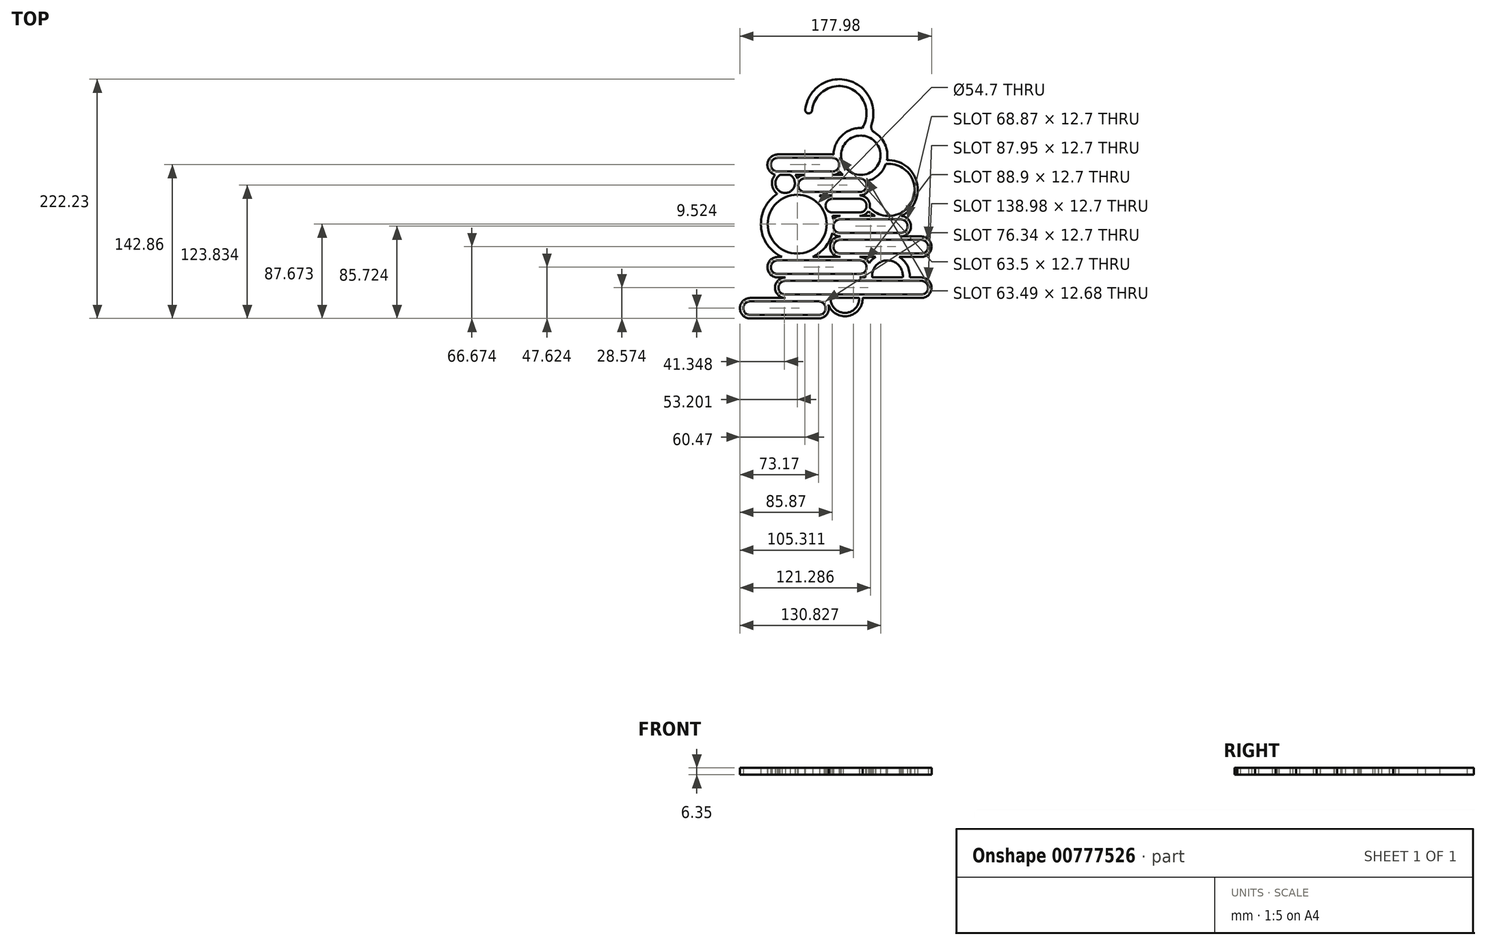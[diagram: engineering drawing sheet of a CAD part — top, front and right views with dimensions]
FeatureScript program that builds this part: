
annotation { "Feature Type Name" : "Feature", "Feature Type Description" : "" }
export const myFeature = defineFeature(function(context is Context, id is Id, definition is map)
    precondition{}
    {
        {
            var Q0;
            Q0=qCreatedBy(makeId("Top.planeOp"),FACE);
            var sketch = newSketch(context, id + "F0", { "sketchPlane" : qUnion([Q0])});
            skLineSegment(sketch, "E0", {"start": v(-38.1, 0) * mm, "end": v(-38.1, -172.32) * mm, "construction": true});
            skArc(sketch, "E1", {"start": v(-38.1, -25.4) * mm, "mid": v(-44.45, -31.75) * mm, "end": v(-38.1, -38.1) * mm});
            skArc(sketch, "E2", {"start": v(-38.1, -22.23) * mm, "mid": v(-47.55, -30.58) * mm, "end": v(-40.43, -40.99) * mm});
            skLineSegment(sketch, "E3", {"start": v(-63.64, -22.23) * mm, "end": v(0, -22.23) * mm, "construction": true});
            skLineSegment(sketch, "E4", {"start": v(-38.1, -22.23) * mm, "end": v(-17.96, -22.23) * mm});
            skLineSegment(sketch, "E5", {"start": v(-35.9, -41.26) * mm, "end": v(-26.48, -41.26) * mm});
            skLineSegment(sketch, "E6", {"start": v(0, 0) * mm, "end": v(-46.92, 0) * mm, "construction": true});
            skLineSegment(sketch, "E7", {"start": v(0, 0) * mm, "end": v(39.73, 0) * mm, "construction": true});
            skLineSegment(sketch, "E8", {"start": v(0, 0) * mm, "end": v(0, -203.37) * mm, "construction": true});
            skLineSegment(sketch, "E9", {"start": v(38.1, 0) * mm, "end": v(38.1, -151.12) * mm, "construction": true});
            skArc(sketch, "E10", {"start": v(38.1, -60.31) * mm, "mid": v(39.65, -60.18) * mm, "end": v(41.15, -59.8) * mm});
            skArc(sketch, "E11", {"start": v(37.6, -57.12) * mm, "mid": v(44.45, -51.02) * mm, "end": v(38.07, -44.44) * mm});
            skLineSegment(sketch, "E12", {"start": v(-35.9, -41.26) * mm, "end": v(-26.48, -41.26) * mm, "construction": true});
            skLineSegment(sketch, "E13", {"start": v(38.1, -50.79) * mm, "end": v(0, -50.79) * mm, "construction": true});
            skLineSegment(sketch, "E14", {"start": v(13.22, -41.26) * mm, "end": v(22.57, -41.26) * mm});
            skLineSegment(sketch, "E15", {"start": v(12.7, -60.31) * mm, "end": v(0.69, -60.31) * mm});
            skLineSegment(sketch, "E16", {"start": v(0, -44.44) * mm, "end": v(38.07, -44.44) * mm});
            skLineSegment(sketch, "E17", {"start": v(37.6, -57.12) * mm, "end": v(0, -57.12) * mm});
            skLineSegment(sketch, "E18", {"start": v(12.7, 0) * mm, "end": v(12.7, -99.3) * mm, "construction": true});
            skArc(sketch, "E19", {"start": v(13.22, -41.26) * mm, "mid": v(16.77, -40.36) * mm, "end": v(19.71, -38.2) * mm});
            skLineSegment(sketch, "E20", {"start": v(-12.7, 0) * mm, "end": v(-12.7, -99.53) * mm, "construction": true});
            skLineSegment(sketch, "E21", {"start": v(0, -44.44) * mm, "end": v(-47.76, -44.44) * mm, "construction": true});
            skArc(sketch, "E22", {"start": v(-12.73, -44.44) * mm, "mid": v(-19.05, -50.56) * mm, "end": v(-13.2, -57.12) * mm});
            skArc(sketch, "E23", {"start": v(-12.7, -41.26) * mm, "mid": v(-16.6, -42.1) * mm, "end": v(-19.83, -44.47) * mm});
            skLineSegment(sketch, "E24", {"start": v(0, -44.44) * mm, "end": v(-12.73, -44.44) * mm});
            skLineSegment(sketch, "E25", {"start": v(0, -57.12) * mm, "end": v(-13.2, -57.12) * mm});
            skLineSegment(sketch, "E26.trimOffspring", {"start": v(13.22, -41.26) * mm, "end": v(22.57, -41.26) * mm, "construction": true});
            skPoint(sketch, "E27.start.orphan", {"position": v(0, -41.38) * mm});
            skPoint(sketch, "E28.start.orphan", {"position": v(0, -28.68) * mm});
            skArc(sketch, "E29", {"start": v(12.7, -38.1) * mm, "mid": v(19.05, -31.75) * mm, "end": v(12.7, -25.4) * mm});
            skLineSegment(sketch, "E30", {"start": v(-38.1, -25.4) * mm, "end": v(12.7, -25.4) * mm});
            skLineSegment(sketch, "E31", {"start": v(-38.1, -38.1) * mm, "end": v(12.7, -38.1) * mm});
            skArc(sketch, "E32", {"start": v(21.8, -28.92) * mm, "mid": v(54.28, -33.2) * mm, "end": v(38.1, -4.72) * mm});
            skArc(sketch, "E33", {"start": v(19.71, -38.2) * mm, "mid": v(21.08, -39.79) * mm, "end": v(22.57, -41.26) * mm});
            skArc(sketch, "E34.trimOffspring", {"start": v(46.59, -46.46) * mm, "mid": v(56.31, -40.62) * mm, "end": v(62.4, -31.04) * mm});
            skLineSegment(sketch, "E35.trimOffspring", {"start": v(38.29, -41.26) * mm, "end": v(45.13, -41.26) * mm, "construction": true});
            skLineSegment(sketch, "E36.trimOffspring", {"start": v(38.1, -41.26) * mm, "end": v(38.29, -41.26) * mm});
            skArc(sketch, "E37", {"start": v(12.7, -63.49) * mm, "mid": v(6.35, -69.84) * mm, "end": v(12.7, -76.19) * mm});
            skArc(sketch, "E38", {"start": v(12.7, -60.31) * mm, "mid": v(8.36, -61.36) * mm, "end": v(4.97, -64.27) * mm});
            skArc(sketch, "E39", {"start": v(38.1, -76.19) * mm, "mid": v(44.45, -69.84) * mm, "end": v(38.1, -63.49) * mm});
            skArc(sketch, "E40", {"start": v(38.1, -79.36) * mm, "mid": v(42.65, -78.2) * mm, "end": v(46.1, -75.02) * mm});
            skLineSegment(sketch, "E41", {"start": v(12.7, -76.19) * mm, "end": v(38.1, -76.19) * mm});
            skLineSegment(sketch, "E42", {"start": v(12.87, -79.36) * mm, "end": v(20.03, -79.36) * mm});
            skLineSegment(sketch, "E43", {"start": v(12.7, -63.49) * mm, "end": v(38.1, -63.49) * mm});
            skArc(sketch, "E44", {"start": v(-35.9, -41.26) * mm, "mid": v(-31.19, -58.04) * mm, "end": v(-26.48, -41.26) * mm});
            skArc(sketch, "E45", {"start": v(-40.43, -40.99) * mm, "mid": v(-43.34, -50.3) * mm, "end": v(-38.5, -58.78) * mm});
            skArc(sketch, "E46.trimOffspring", {"start": v(-19.83, -44.47) * mm, "mid": v(-20.65, -42.8) * mm, "end": v(-21.71, -41.26) * mm});
            skCircle(sketch, "E47", {"center": v(-19.97, -86.94) * mm, "radius": 27.35 * mm});
            skLineSegment(sketch, "E48", {"start": v(76.2, 0) * mm, "end": v(76.2, -88.89) * mm, "construction": true});
            skArc(sketch, "E49", {"start": v(76.2, -95.24) * mm, "mid": v(82.55, -88.89) * mm, "end": v(76.2, -82.54) * mm});
            skArc(sketch, "E50", {"start": v(76.2, -98.41) * mm, "mid": v(85.72, -89.13) * mm, "end": v(76.69, -79.37) * mm});
            skLineSegment(sketch, "E51", {"start": v(12.87, -79.36) * mm, "end": v(20.03, -79.36) * mm, "construction": true});
            skArc(sketch, "E52", {"start": v(20.03, -82.54) * mm, "mid": v(13.68, -88.89) * mm, "end": v(20.03, -95.24) * mm});
            skArc(sketch, "E53", {"start": v(20.03, -79.36) * mm, "mid": v(16.44, -80.06) * mm, "end": v(13.38, -82.07) * mm});
            skLineSegment(sketch, "E54", {"start": v(65.4, -79.36) * mm, "end": v(38.1, -79.36) * mm});
            skLineSegment(sketch, "E55", {"start": v(20.03, -88.89) * mm, "end": v(20.03, -107.94) * mm, "construction": true});
            skLineSegment(sketch, "E56", {"start": v(20.03, -95.24) * mm, "end": v(76.2, -95.24) * mm});
            skLineSegment(sketch, "E57", {"start": v(20.03, -82.54) * mm, "end": v(76.2, -82.54) * mm});
            skLineSegment(sketch, "E58.trimOffspring", {"start": v(38.1, -79.36) * mm, "end": v(52.43, -79.36) * mm, "construction": true});
            skLineSegment(sketch, "E59.trimOffspring", {"start": v(49.17, -41.26) * mm, "end": v(58.95, -41.26) * mm, "construction": true});
            skArc(sketch, "E60.trimOffspring", {"start": v(63.33, -27.5) * mm, "mid": v(60.3, -10.42) * mm, "end": v(46.8, 0.43) * mm});
            skArc(sketch, "E61.trimOffspring", {"start": v(41.15, -59.8) * mm, "mid": v(46.92, -54.38) * mm, "end": v(46.59, -46.46) * mm});
            skArc(sketch, "E62.trimOffspring", {"start": v(41.4, -60.9) * mm, "mid": v(39.77, -60.46) * mm, "end": v(38.1, -60.31) * mm});
            skArc(sketch, "E63", {"start": v(-38.5, -58.78) * mm, "mid": v(-53.58, -89.37) * mm, "end": v(-34.25, -117.46) * mm});
            skPoint(sketch, "E64.orphan", {"position": v(0, -60.31) * mm});
            skArc(sketch, "E65.trimOffspring", {"start": v(4.97, -64.27) * mm, "mid": v(2.91, -62.2) * mm, "end": v(0.69, -60.31) * mm});
            skArc(sketch, "E66.trimOffspring", {"start": v(13.38, -82.07) * mm, "mid": v(13.15, -80.71) * mm, "end": v(12.87, -79.36) * mm});
            skArc(sketch, "E67.trimOffspring", {"start": v(12.75, -95.02) * mm, "mid": v(16.01, -97.52) * mm, "end": v(20.03, -98.41) * mm});
            skArc(sketch, "E68.trimOffspring", {"start": v(46.1, -75.02) * mm, "mid": v(49.1, -77.41) * mm, "end": v(52.43, -79.36) * mm});
            skArc(sketch, "E69", {"start": v(41.4, -60.9) * mm, "mid": v(46.45, -65.25) * mm, "end": v(47.4, -71.86) * mm});
            skArc(sketch, "E70.trimOffspring", {"start": v(47.4, -71.86) * mm, "mid": v(87.68, -63.49) * mm, "end": v(62.4, -31.04) * mm});
            skArc(sketch, "E71.trimOffspring", {"start": v(76.69, -79.37) * mm, "mid": v(91.08, -48.01) * mm, "end": v(63.33, -27.5) * mm});
            skLineSegment(sketch, "E72.trimOffspring", {"start": v(76.2, -79.36) * mm, "end": v(95.28, -79.36) * mm, "construction": true});
            skLineSegment(sketch, "E73", {"start": v(12.7, -25.4) * mm, "end": v(50.72, -25.4) * mm, "construction": true});
            skLineSegment(sketch, "E74", {"start": v(-0.45, 15.88) * mm, "end": v(-52.81, 15.88) * mm, "construction": true});
            skLineSegment(sketch, "E75.trimOffspring", {"start": v(14.62, -22.23) * mm, "end": v(38.77, -22.23) * mm, "construction": true});
            skLineSegment(sketch, "E76", {"start": v(-17.96, -22.23) * mm, "end": v(12.7, -22.23) * mm});
            skLineSegment(sketch, "E77", {"start": v(-0.45, 15.88) * mm, "end": v(19.05, 15.88) * mm, "construction": true});
            skLineSegment(sketch, "E78", {"start": v(19.05, 15.88) * mm, "end": v(19.05, -22.23) * mm, "construction": true});
            skArc(sketch, "E79", {"start": v(-6.35, 15.88) * mm, "mid": v(26.07, 40.28) * mm, "end": v(40.56, 2.37) * mm});
            skArc(sketch, "E80", {"start": v(-12.7, 15.88) * mm, "mid": v(27.03, 46.6) * mm, "end": v(46.8, 0.43) * mm});
            skLineSegment(sketch, "E81", {"start": v(-12.7, 15.88) * mm, "end": v(-6.35, 15.88) * mm});
            skArc(sketch, "E82", {"start": v(12.7, -22.23) * mm, "mid": v(13.2, -22.24) * mm, "end": v(13.71, -22.28) * mm});
            skArc(sketch, "E83", {"start": v(38.1, -4.72) * mm, "mid": v(23.93, -12.77) * mm, "end": v(21.8, -28.92) * mm});
            skArc(sketch, "E84.trimOffspring", {"start": v(38.1, -41.25) * mm, "mid": v(38.2, -41.26) * mm, "end": v(38.29, -41.26) * mm});
            skArc(sketch, "E85", {"start": v(13.71, -22.28) * mm, "mid": v(21.92, -4.27) * mm, "end": v(40.56, 2.37) * mm});
            skLineSegment(sketch, "E86", {"start": v(95.28, -79.36) * mm, "end": v(95.28, -160.34) * mm, "construction": true});
            skLineSegment(sketch, "E87", {"start": v(76.2, -98.41) * mm, "end": v(117.6, -98.41) * mm, "construction": true});
            skLineSegment(sketch, "E88.trimOffspring", {"start": v(-21.71, -41.26) * mm, "end": v(-12.7, -41.26) * mm, "construction": true});
            skLineSegment(sketch, "E89.trimOffspring", {"start": v(-21.71, -41.26) * mm, "end": v(-12.7, -41.26) * mm});
            skArc(sketch, "E90", {"start": v(95.28, -114.29) * mm, "mid": v(101.63, -107.94) * mm, "end": v(95.28, -101.59) * mm});
            skArc(sketch, "E91", {"start": v(95.28, -117.46) * mm, "mid": v(104.8, -107.94) * mm, "end": v(95.28, -98.41) * mm});
            skArc(sketch, "E92", {"start": v(20.03, -101.59) * mm, "mid": v(13.68, -107.94) * mm, "end": v(20.03, -114.29) * mm});
            skArc(sketch, "E93", {"start": v(20.03, -98.41) * mm, "mid": v(10.5, -107.94) * mm, "end": v(20.03, -117.46) * mm});
            skLineSegment(sketch, "E94", {"start": v(20.03, -107.94) * mm, "end": v(20.03, -131.39) * mm, "construction": true});
            skLineSegment(sketch, "E95", {"start": v(38.1, -117.46) * mm, "end": v(52.9, -117.46) * mm});
            skLineSegment(sketch, "E96", {"start": v(20.03, -114.29) * mm, "end": v(95.28, -114.29) * mm});
            skLineSegment(sketch, "E97", {"start": v(20.03, -101.59) * mm, "end": v(95.28, -101.59) * mm});
            skLineSegment(sketch, "E98", {"start": v(76.2, -98.41) * mm, "end": v(95.28, -98.41) * mm});
            skLineSegment(sketch, "E99", {"start": v(76.2, -88.89) * mm, "end": v(76.2, -150.34) * mm, "construction": true});
            skArc(sketch, "E100", {"start": v(-38.1, -120.64) * mm, "mid": v(-44.45, -126.99) * mm, "end": v(-38.1, -133.34) * mm});
            skArc(sketch, "E101", {"start": v(-38.1, -117.46) * mm, "mid": v(-47.63, -126.99) * mm, "end": v(-38.1, -136.51) * mm});
            skLineSegment(sketch, "E102", {"start": v(20.03, -117.46) * mm, "end": v(-5.69, -117.46) * mm, "construction": true});
            skArc(sketch, "E103", {"start": v(38.1, -133.34) * mm, "mid": v(44.45, -126.99) * mm, "end": v(38.1, -120.64) * mm});
            skArc(sketch, "E104", {"start": v(38.1, -136.51) * mm, "mid": v(40.79, -136.12) * mm, "end": v(43.26, -135) * mm});
            skLineSegment(sketch, "E105", {"start": v(-38.1, -117.46) * mm, "end": v(-34.25, -117.46) * mm});
            skLineSegment(sketch, "E106", {"start": v(-31, -120.64) * mm, "end": v(38.1, -120.64) * mm});
            skLineSegment(sketch, "E107", {"start": v(-38.1, -136.51) * mm, "end": v(-31, -136.51) * mm});
            skLineSegment(sketch, "E108", {"start": v(-38.1, -133.34) * mm, "end": v(38.1, -133.34) * mm});
            skLineSegment(sketch, "E109", {"start": v(-31, -120.64) * mm, "end": v(-38.1, -120.64) * mm});
            skLineSegment(sketch, "E110.trimOffspring", {"start": v(-34.25, -117.46) * mm, "end": v(-92.83, -117.46) * mm, "construction": true});
            skArc(sketch, "E111.trimOffspring", {"start": v(-5.69, -117.46) * mm, "mid": v(6.07, -108.33) * mm, "end": v(12.75, -95.02) * mm});
            skLineSegment(sketch, "E112.trimOffspring", {"start": v(-5.69, -117.46) * mm, "end": v(20.03, -117.46) * mm});
            skArc(sketch, "E113", {"start": v(52.9, -117.46) * mm, "mid": v(49.58, -120.05) * mm, "end": v(46.87, -123.26) * mm});
            skLineSegment(sketch, "E114.trimOffspring", {"start": v(74.9, -117.46) * mm, "end": v(95.28, -117.46) * mm});
            skArc(sketch, "E115.trimOffspring", {"start": v(43.26, -135) * mm, "mid": v(43.27, -135.75) * mm, "end": v(43.32, -136.51) * mm});
            skArc(sketch, "E116.trimOffspring", {"start": v(46.87, -123.26) * mm, "mid": v(43.36, -119.04) * mm, "end": v(38.1, -117.46) * mm});
            skLineSegment(sketch, "E117", {"start": v(-31, -120.64) * mm, "end": v(-31, -173.3) * mm, "construction": true});
            skArc(sketch, "E118", {"start": v(-31, -139.69) * mm, "mid": v(-37.35, -146.04) * mm, "end": v(-31, -152.39) * mm});
            skArc(sketch, "E119", {"start": v(-31, -136.51) * mm, "mid": v(-40.53, -146.04) * mm, "end": v(-31, -155.56) * mm});
            skArc(sketch, "E120", {"start": v(95.28, -152.39) * mm, "mid": v(101.63, -146.04) * mm, "end": v(95.28, -139.69) * mm});
            skArc(sketch, "E121", {"start": v(95.28, -155.56) * mm, "mid": v(104.8, -146.04) * mm, "end": v(95.28, -136.51) * mm});
            skLineSegment(sketch, "E122", {"start": v(38.1, -136.51) * mm, "end": v(43.32, -136.51) * mm, "construction": true});
            skLineSegment(sketch, "E123", {"start": v(38.1, -136.51) * mm, "end": v(43.32, -136.51) * mm});
            skLineSegment(sketch, "E124", {"start": v(0, -155.56) * mm, "end": v(7.94, -155.56) * mm});
            skLineSegment(sketch, "E125", {"start": v(-31, -152.39) * mm, "end": v(95.28, -152.39) * mm});
            skLineSegment(sketch, "E126", {"start": v(76.2, -139.69) * mm, "end": v(-31, -139.69) * mm});
            skLineSegment(sketch, "E127", {"start": v(76.2, -139.69) * mm, "end": v(95.28, -139.69) * mm});
            skArc(sketch, "E128.trimOffspring", {"start": v(84.47, -136.51) * mm, "mid": v(82.33, -125.65) * mm, "end": v(74.9, -117.46) * mm});
            skLineSegment(sketch, "E129.trimOffspring", {"start": v(49.7, -136.51) * mm, "end": v(78.1, -136.51) * mm, "construction": true});
            skLineSegment(sketch, "E130.trimOffspring", {"start": v(49.7, -136.51) * mm, "end": v(78.1, -136.51) * mm});
            skArc(sketch, "E131.trimOffspring", {"start": v(78.1, -136.51) * mm, "mid": v(63.9, -120.64) * mm, "end": v(49.7, -136.51) * mm});
            skLineSegment(sketch, "E132.trimOffspring", {"start": v(84.47, -136.51) * mm, "end": v(130.9, -136.51) * mm, "construction": true});
            skLineSegment(sketch, "E133.trimOffspring", {"start": v(84.47, -136.51) * mm, "end": v(95.28, -136.51) * mm});
            skArc(sketch, "E134", {"start": v(11.12, -155.56) * mm, "mid": v(24.38, -169.4) * mm, "end": v(37.64, -155.56) * mm});
            skArc(sketch, "E135", {"start": v(7.94, -155.56) * mm, "mid": v(24.38, -172.58) * mm, "end": v(40.81, -155.56) * mm});
            skLineSegment(sketch, "E136", {"start": v(-63.64, -22.22) * mm, "end": v(-63.64, -171.44) * mm, "construction": true});
            skArc(sketch, "E137", {"start": v(-63.64, -158.74) * mm, "mid": v(-70, -165.09) * mm, "end": v(-63.64, -171.44) * mm});
            skArc(sketch, "E138", {"start": v(-63.64, -155.56) * mm, "mid": v(-73.17, -165.09) * mm, "end": v(-63.64, -174.61) * mm});
            skLineSegment(sketch, "E139", {"start": v(-31, -155.56) * mm, "end": v(-120.7, -155.56) * mm, "construction": true});
            skArc(sketch, "E140", {"start": v(0, -171.44) * mm, "mid": v(6.35, -165.09) * mm, "end": v(0, -158.74) * mm});
            skArc(sketch, "E141", {"start": v(0, -174.61) * mm, "mid": v(9.53, -165.09) * mm, "end": v(0, -155.56) * mm});
            skLineSegment(sketch, "E142", {"start": v(-63.64, -155.56) * mm, "end": v(-31, -155.56) * mm});
            skLineSegment(sketch, "E143", {"start": v(-63.64, -158.74) * mm, "end": v(0, -158.74) * mm});
            skLineSegment(sketch, "E144", {"start": v(-63.64, -174.61) * mm, "end": v(0, -174.61) * mm});
            skLineSegment(sketch, "E145", {"start": v(-63.64, -171.44) * mm, "end": v(0, -171.44) * mm});
            skLineSegment(sketch, "E146.trimOffspring", {"start": v(40.81, -155.56) * mm, "end": v(95.28, -155.56) * mm});
            skLineSegment(sketch, "E147.trimOffspring", {"start": v(11.12, -155.56) * mm, "end": v(37.64, -155.56) * mm});
            skSolve(sketch);
        }
        {
            var Q0;
            Q0 = qSketchRegion(id + "F0", true);
            extrude(context, id + "F1", {"entities" : qUnion([Q0]), "depth" : 6.35 * mm, "offsetDistance" : 25.4 * mm});
        }
        {
            var Q0;
            Q0=makeQuery(id+"F1.opExtrude","SWEPT_EDGE",EDGE,{"disambiguationData":[OSD([sQuery(id+"F0.wireOp",EDGE,"E32"),sQuery(id+"F0.wireOp",EDGE,"FV0pCvqx-ffxO-Eyq5-4q0J-zGdBt2hZ4NIG")])]});
            var Q1;
            Q1=makeQuery(id+"F1.opExtrude","SWEPT_EDGE",EDGE,{"disambiguationData":[OSD([sQuery(id+"F0.wireOp",EDGE,"E60.trimOffspring"),sQuery(id+"F0.wireOp",EDGE,"E80")])]});
            fillet(context, id + "F2", {"entities" : qUnion([Q0, Q1]), "radius" : 6.35 * mm, "tangentPropagation" : true, "allowEdgeOverflow" : false});
        }
        {
            var Q0;
            Q0=makeQuery(id+"F1.opExtrude","SWEPT_EDGE",EDGE,{"disambiguationData":[OSD([sQuery(id+"F0.wireOp",EDGE,"E80"),sQuery(id+"F0.wireOp",EDGE,"E81")])]});
            var Q1;
            Q1=makeQuery(id+"F1.opExtrude","SWEPT_EDGE",EDGE,{"disambiguationData":[OSD([sQuery(id+"F0.wireOp",EDGE,"E79"),sQuery(id+"F0.wireOp",EDGE,"E81")])]});
            fillet(context, id + "F3", {"entities" : qUnion([Q0, Q1]), "radius" : 3.17 * mm, "tangentPropagation" : true, "allowEdgeOverflow" : false});
        }
    });
